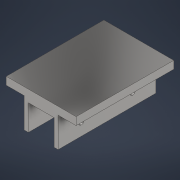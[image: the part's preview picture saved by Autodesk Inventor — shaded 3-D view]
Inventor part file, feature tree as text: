
AUTODESK INVENTOR PART (.ipt)
format: ipt  version: 2021 (Build 250183000, 183)  size: 195,584 bytes
history: native  units: mm
features: sketch x4, extrude x3, hole x1
ambient origin geometry x8: Origin, YZ Plane, XZ Plane, XY Plane, X Axis, Y Axis, Z Axis, Center Point
bodies: Solid1 (feature_tree)
feature tree (8):
  extrude  "clamp_base"  Depth=66.0mm
  extrude  "clamp_extrusion"  TaperAngle=0.0deg  [1 undecoded]
  extrude  "platform"  Depth=50.0mm
  hole  "clampHole"  [1 undecoded]
  sketch  "Sketch1"  dims[d0=58.0mm d1=66.0mm]
  sketch  "Sketch2"  dims[d2=33.0mm d3=0.0mm]
  sketch  "Sketch4"  dims[d4=190.0mm d5=0.0mm d6=50.0mm]
  sketch  "Sketch8"  dims[d7=50.0mm d8=25.0mm d9=0.0mm d10=0.0mm d12=1120.0mm d13=15.0mm d14=0.0mm d15=80.0mm d35=0.0mm d36=0.0mm d37=35.0mm d38=35.0mm d51=45.0mm d53=10.0mm d54=6.0mm d55=4.0mm d56=2.0mm d57=90.0deg d58=8.0mm d59=20.594885mm d60=100.0mm d61=190.0mm]
note: 2 required parameter values undecoded (feature->parameter linkage not recoverable at this tier; creation-order binding heuristic only, values carry confidence <= 0.55)
